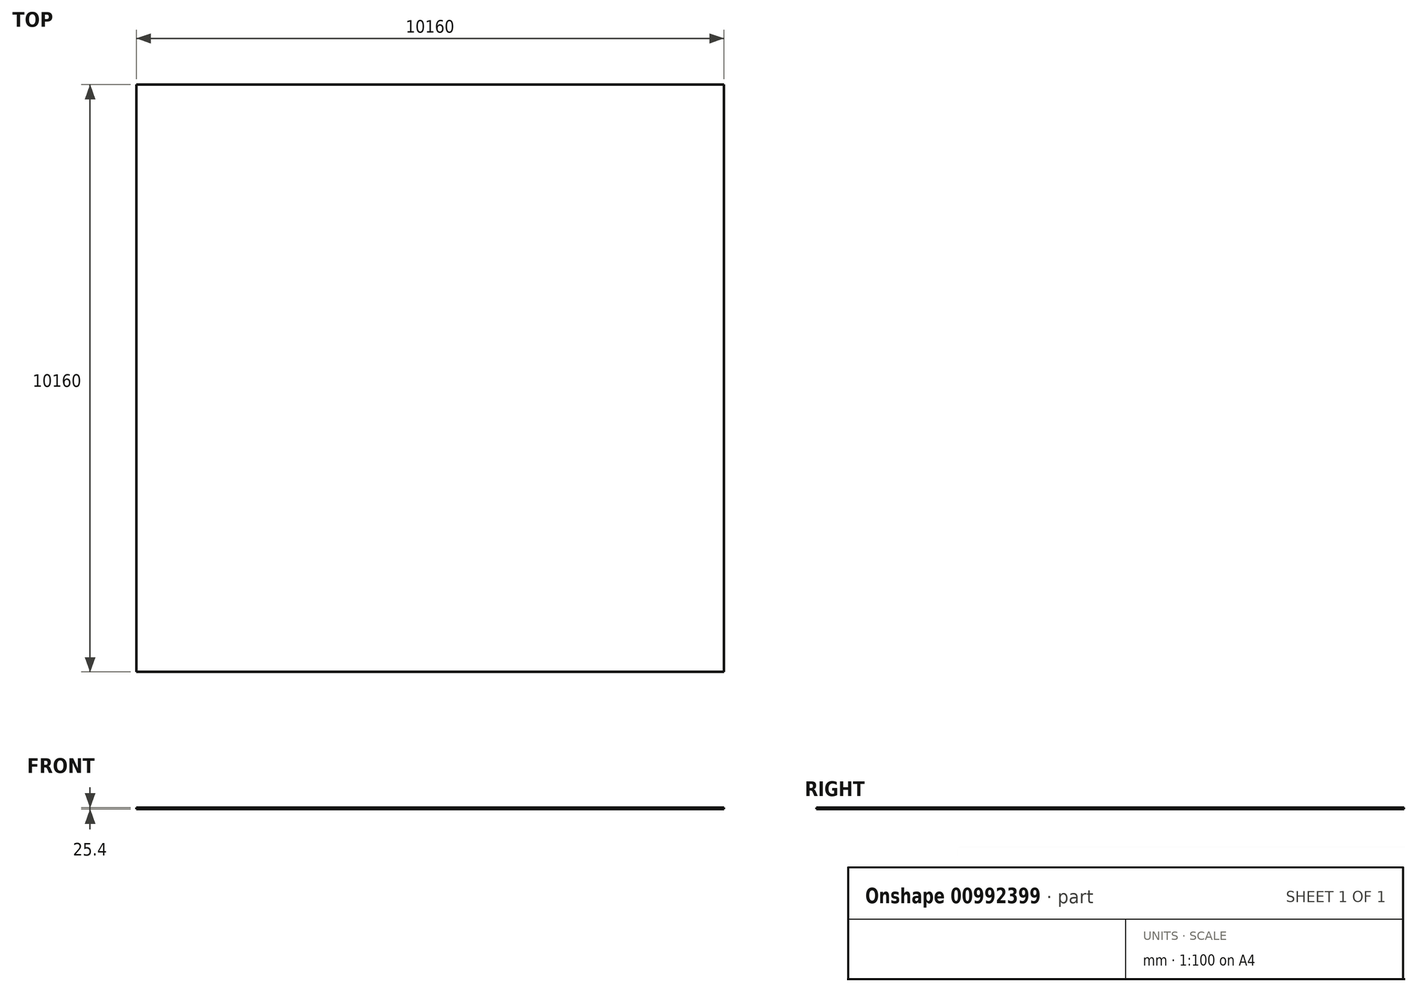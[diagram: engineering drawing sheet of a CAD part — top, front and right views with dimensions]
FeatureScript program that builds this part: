
annotation { "Feature Type Name" : "Feature", "Feature Type Description" : "" }
export const myFeature = defineFeature(function(context is Context, id is Id, definition is map)
    precondition{}
    {
        {
            var Q0;
            Q0=qCreatedBy(makeId("Top.planeOp"),FACE);
            var sketch = newSketch(context, id + "F0", { "sketchPlane" : qUnion([Q0])});
            skLineSegment(sketch, "E0.bottom", {"start": v(5080, 5080) * mm, "end": v(-5080, 5080) * mm});
            skLineSegment(sketch, "E0.top", {"start": v(5080, -5080) * mm, "end": v(-5080, -5080) * mm});
            skLineSegment(sketch, "E0.left", {"start": v(5080, 5080) * mm, "end": v(5080, -5080) * mm});
            skLineSegment(sketch, "E0.right", {"start": v(-5080, 5080) * mm, "end": v(-5080, -5080) * mm});
            skPoint(sketch, "E0.middle", {"position": v(0, 0) * mm});
            skSolve(sketch);
        }
        {
            var Q0;
            Q0=makeQuery(id+"F0.imprint","IMPRINT",FACE,{"disambiguationData":[TD([[makeQuery(id+"F0.imprint","IMPRINT",EDGE,{"derivedFrom":sQuery(id+"F0.wireOp",EDGE,"E0.bottom")}),1.0]])]});
            extrude(context, id + "F1", {"entities" : qUnion([Q0]), "depth" : 25.4 * mm, "offsetDistance" : 25.4 * mm});
        }
    });
